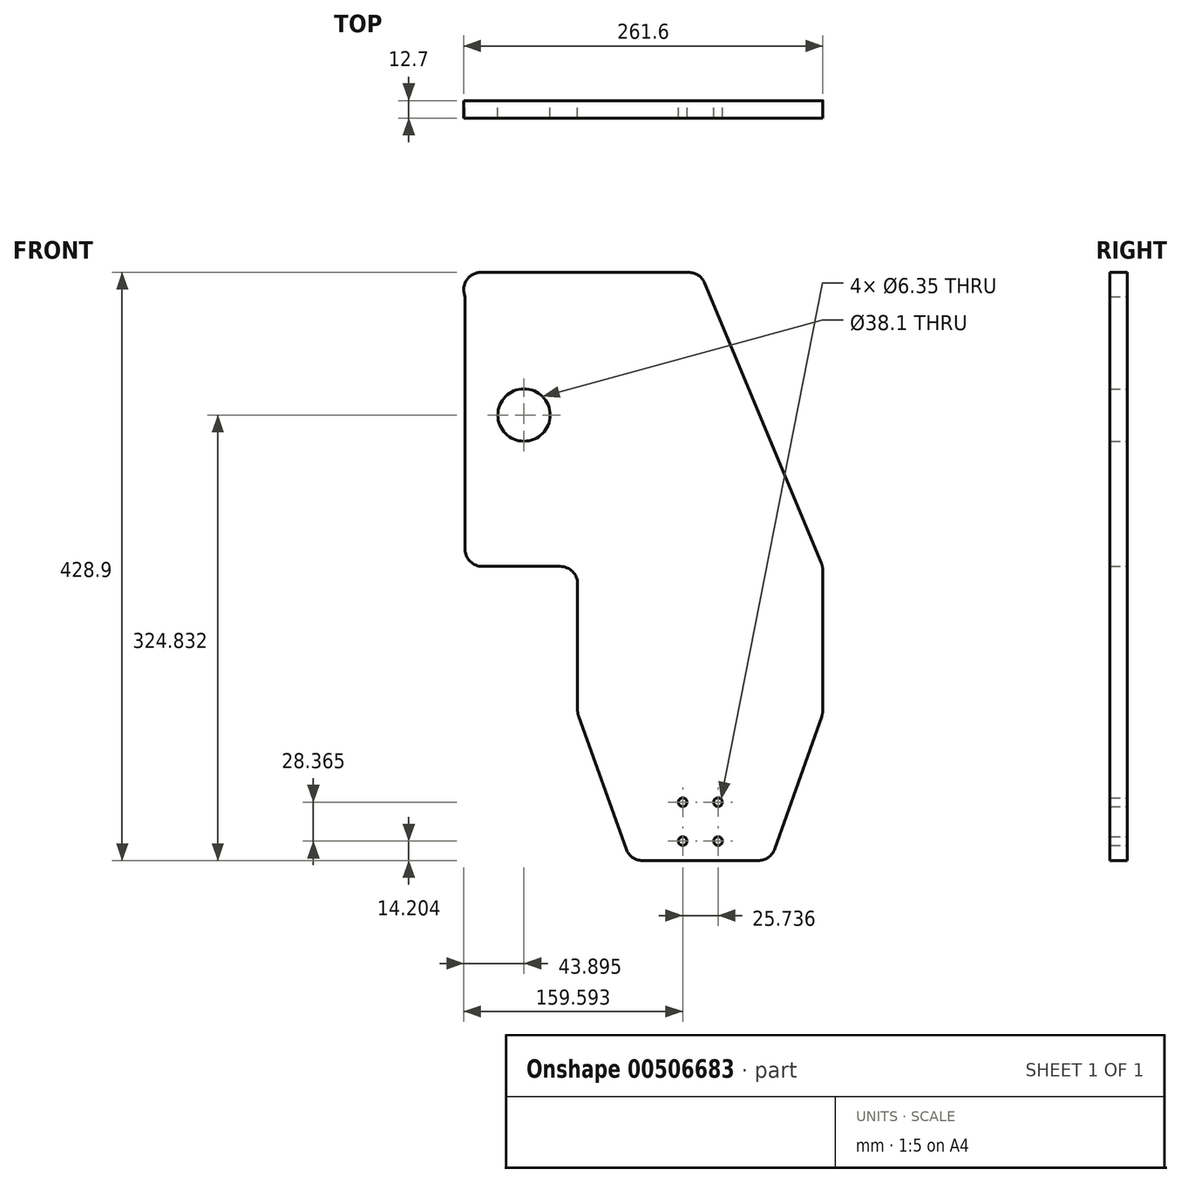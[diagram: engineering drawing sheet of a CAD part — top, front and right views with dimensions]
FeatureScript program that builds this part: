
annotation { "Feature Type Name" : "Feature", "Feature Type Description" : "" }
export const myFeature = defineFeature(function(context is Context, id is Id, definition is map)
    precondition{}
    {
        {
            var Q0;
            Q0=qCreatedBy(makeId("Front.planeOp"),FACE);
            var sketch = newSketch(context, id + "F0", { "sketchPlane" : qUnion([Q0])});
            skLineSegment(sketch, "E0.bottom", {"start": v(-8.47, 214.45) * mm, "end": v(-89.3, 214.45) * mm});
            skLineSegment(sketch, "E0.top", {"start": v(42.32, -214.45) * mm, "end": v(-41.97, -214.45) * mm});
            skLineSegment(sketch, "E0.left", {"start": v(89.3, -2.54) * mm, "end": v(89.3, -105.04) * mm});
            skLineSegment(sketch, "E0.right", {"start": v(-89.3, -12.7) * mm, "end": v(-89.3, -105.02) * mm});
            skPoint(sketch, "E0.middle", {"position": v(0, 0) * mm});
            skLineSegment(sketch, "E1", {"start": v(-159.6, 214.45) * mm, "end": v(-89.3, 214.45) * mm});
            skLineSegment(sketch, "E2", {"start": v(3.26, 206.63) * mm, "end": v(88.33, 2.34) * mm});
            skPoint(sketch, "E3.orphan", {"position": v(89.3, 214.45) * mm});
            skLineSegment(sketch, "E4", {"start": v(-88.56, -109.3) * mm, "end": v(-53.93, -206.03) * mm});
            skLineSegment(sketch, "E5", {"start": v(88.57, -109.28) * mm, "end": v(54.29, -205.99) * mm});
            skPoint(sketch, "E6.end.orphan", {"position": v(-50.91, -107.16) * mm});
            skPoint(sketch, "E7.end.orphan", {"position": v(51.29, -107.16) * mm});
            skPoint(sketch, "E8.orphan", {"position": v(-89.3, -214.45) * mm});
            skPoint(sketch, "E9.orphan", {"position": v(89.3, -214.45) * mm});
            skPoint(sketch, "E10.visualSharp", {"position": v(-178.6, 214.45) * mm});
            skArc(sketch, "E10.filletArc", {"start": v(-159.6, 214.45) * mm, "mid": v(-170.2, 208.73) * mm, "end": v(-171.27, 196.73) * mm});
            skPoint(sketch, "E11.visualSharp", {"position": v(0, 214.45) * mm});
            skArc(sketch, "E11.filletArc", {"start": v(3.26, 206.63) * mm, "mid": v(-1.42, 212.31) * mm, "end": v(-8.47, 214.45) * mm});
            skPoint(sketch, "E12.visualSharp", {"position": v(51.29, -214.45) * mm});
            skArc(sketch, "E12.filletArc", {"start": v(42.32, -214.45) * mm, "mid": v(49.64, -212.12) * mm, "end": v(54.29, -205.99) * mm});
            skPoint(sketch, "E13.visualSharp", {"position": v(-50.91, -214.45) * mm});
            skArc(sketch, "E13.filletArc", {"start": v(-53.93, -206.03) * mm, "mid": v(-49.28, -212.13) * mm, "end": v(-41.97, -214.45) * mm});
            skLineSegment(sketch, "E14", {"start": v(-171.27, 196.73) * mm, "end": v(-171.27, 12.7) * mm});
            skLineSegment(sketch, "E15", {"start": v(-158.57, 0) * mm, "end": v(-102, 0) * mm});
            skPoint(sketch, "E16.visualSharp", {"position": v(-171.27, 0) * mm});
            skArc(sketch, "E16.filletArc", {"start": v(-171.27, 12.7) * mm, "mid": v(-167.55, 3.72) * mm, "end": v(-158.57, 0) * mm});
            skPoint(sketch, "E17.visualSharp", {"position": v(-89.3, 0) * mm});
            skArc(sketch, "E17.filletArc", {"start": v(-89.3, -12.7) * mm, "mid": v(-93.02, -3.72) * mm, "end": v(-102, 0) * mm});
            skPoint(sketch, "E18.visualSharp", {"position": v(89.3, 0) * mm});
            skArc(sketch, "E18.filletArc", {"start": v(89.3, -2.54) * mm, "mid": v(89.06, -0.05) * mm, "end": v(88.33, 2.34) * mm});
            skPoint(sketch, "E19.visualSharp", {"position": v(89.3, -107.22) * mm});
            skArc(sketch, "E19.filletArc", {"start": v(88.57, -109.28) * mm, "mid": v(89.12, -107.2) * mm, "end": v(89.3, -105.04) * mm});
            skPoint(sketch, "E20.visualSharp", {"position": v(-89.3, -107.22) * mm});
            skArc(sketch, "E20.filletArc", {"start": v(-89.3, -105.02) * mm, "mid": v(-89.12, -107.2) * mm, "end": v(-88.56, -109.3) * mm});
            skLineSegment(sketch, "E21", {"start": v(0.17, -214.45) * mm, "end": v(0, 0) * mm, "construction": true});
            skLineSegment(sketch, "E22", {"start": v(-89.3, -105.02) * mm, "end": v(89.3, -105.04) * mm, "construction": true});
            skLineSegment(sketch, "E23", {"start": v(-71.24, -157.66) * mm, "end": v(71.43, -157.64) * mm, "construction": true});
            skLineSegment(sketch, "E24", {"start": v(-12.66, -171.85) * mm, "end": v(-12.7, -171.9) * mm, "construction": true});
            skLineSegment(sketch, "E25", {"start": v(0.1, -157.65) * mm, "end": v(0.13, -157.69) * mm, "construction": true});
            skCircle(sketch, "E26", {"center": v(-12.7, -200.25) * mm, "radius": 3.18 * mm});
            skCircle(sketch, "E27", {"center": v(-12.7, -171.9) * mm, "radius": 3.18 * mm});
            skCircle(sketch, "E28.MirrorC", {"center": v(12.98, -171.88) * mm, "radius": 3.18 * mm});
            skCircle(sketch, "E29.MirrorC", {"center": v(13.03, -200.23) * mm, "radius": 3.18 * mm});
            skLineSegment(sketch, "E30.trimOffspring", {"start": v(49.36, -212.31) * mm, "end": v(51.29, -214.45) * mm, "construction": true});
            skLineSegment(sketch, "E31.trimOffspring", {"start": v(-49, -212.32) * mm, "end": v(-50.91, -214.45) * mm, "construction": true});
            skPoint(sketch, "E32.orphan", {"position": v(-25.41, -200.25) * mm});
            skPoint(sketch, "E33.end.orphan", {"position": v(25.7, -200.25) * mm});
            skPoint(sketch, "E34.orphan", {"position": v(25.7, -186.05) * mm});
            skPoint(sketch, "E35.end.orphan", {"position": v(25.7, -214.45) * mm});
            skPoint(sketch, "E36.orphan", {"position": v(-25.41, -186.05) * mm});
            skPoint(sketch, "E37.end.orphan", {"position": v(-25.41, -214.45) * mm});
            skCircle(sketch, "E38", {"center": v(-128.4, 110.38) * mm, "radius": 19.05 * mm});
            skSolve(sketch);
        }
        {
            var Q0;
            Q0=makeQuery(id+"F0.imprint","IMPRINT",FACE,{"disambiguationData":[TD([[makeQuery(id+"F0.imprint","IMPRINT",EDGE,{"derivedFrom":sQuery(id+"F0.wireOp",EDGE,"E0.bottom")}),1.0]])]});
            extrude(context, id + "F1", {"entities" : qUnion([Q0]), "depth" : 12.7 * mm});
        }
    });
